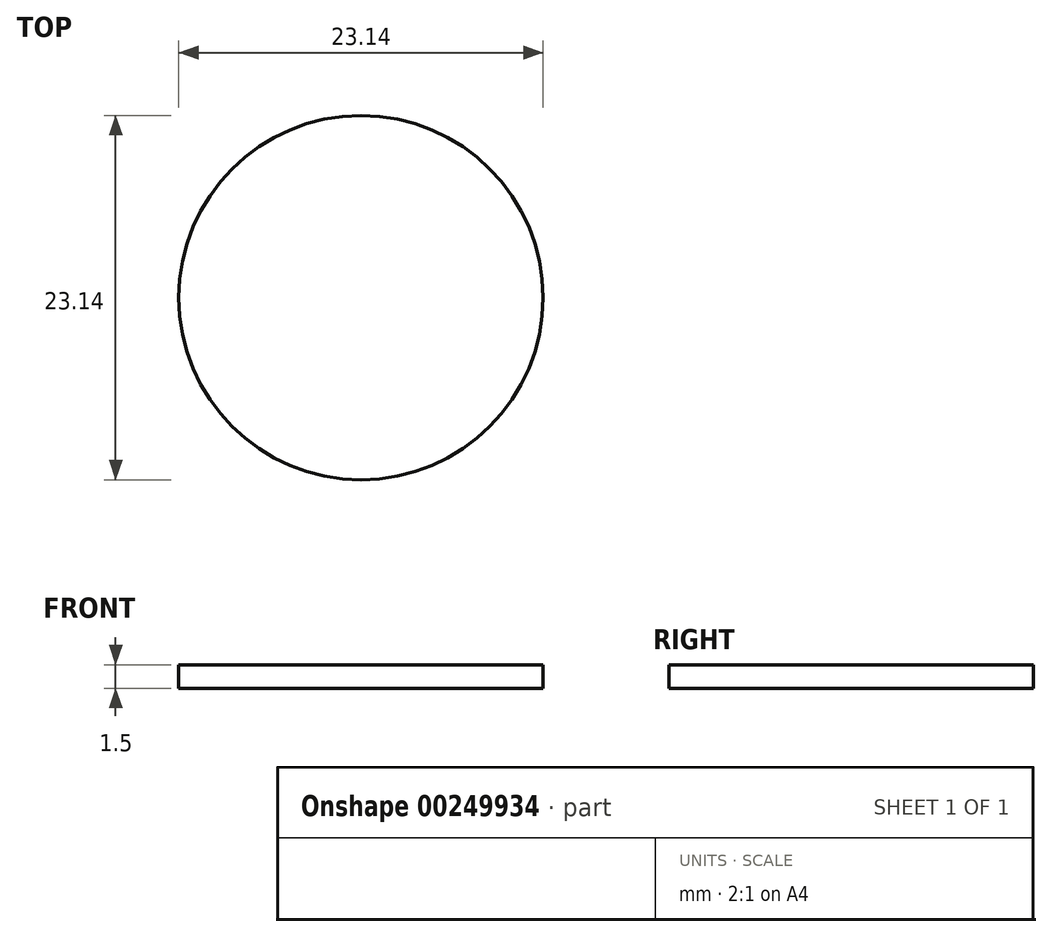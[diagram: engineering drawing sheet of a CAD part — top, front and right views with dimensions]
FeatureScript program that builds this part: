
annotation { "Feature Type Name" : "Feature", "Feature Type Description" : "" }
export const myFeature = defineFeature(function(context is Context, id is Id, definition is map)
    precondition{}
    {
        {
            var Q0;
            Q0=qCreatedBy(makeId("Top.planeOp"),FACE);
            var sketch = newSketch(context, id + "F0", { "sketchPlane" : qUnion([Q0])});
            skCircle(sketch, "E0", {"center": v(0, 0) * mm, "radius": 11.57 * mm});
            skSolve(sketch);
        }
        {
            var Q0;
            Q0=qSketchRegion(id+"F0",true);
            extrude(context, id + "F1", {"entities" : qUnion([Q0]), "depth" : 1.5 * mm});
        }
    });
